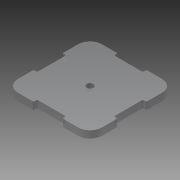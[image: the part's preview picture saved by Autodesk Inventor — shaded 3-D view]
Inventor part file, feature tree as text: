
AUTODESK INVENTOR PART (.ipt)
format: ipt  version: 2015 (Build 190159000, 159)  size: 137,728 bytes
history: native  units: mm
features: extrude x1, sketch x1
ambient origin geometry x8: Origin, YZ Plane, XZ Plane, XY Plane, X Axis, Y Axis, Z Axis, Center Point
bodies: Body1 (feature_tree)
feature tree (2):
  extrude  "Extrusion6"  Depth=3.0mm
  sketch  "Sketch1"  dims[d0=31.75mm d11=10.0mm d12=5.0mm d15=36.0mm d17=16.0mm d19=18.0mm d20=18.0mm d39=35.0mm d44=12.0mm d45=0.5mm d46=40.0mm d48=360.0deg d50=5.0mm d53=2.8mm d54=3.0mm d55=0.0mm]
